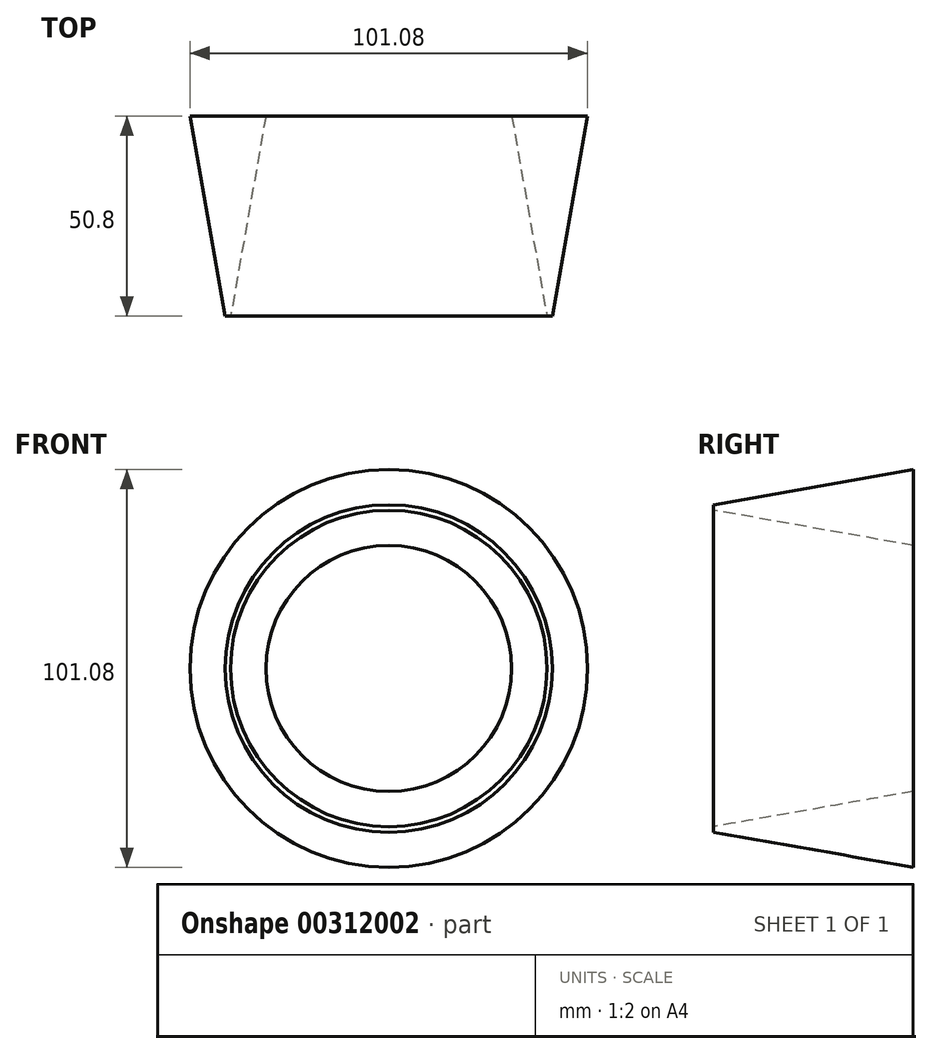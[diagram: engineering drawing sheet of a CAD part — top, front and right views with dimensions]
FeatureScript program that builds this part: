
annotation { "Feature Type Name" : "Feature", "Feature Type Description" : "" }
export const myFeature = defineFeature(function(context is Context, id is Id, definition is map)
    precondition{}
    {
        {
            var Q0;
            Q0=qCreatedBy(makeId("Front.planeOp"),FACE);
            var sketch = newSketch(context, id + "F0", { "sketchPlane" : qUnion([Q0])});
            skCircle(sketch, "E0", {"center": v(-5.39, 0) * mm, "radius": 31.23 * mm});
            skCircle(sketch, "E1", {"center": v(-5.39, 0) * mm, "radius": 50.54 * mm});
            skSolve(sketch);
        }
        {
            var Q0;
            Q0=makeQuery(id+"F0.imprint","IMPRINT",FACE,{"disambiguationData":[TD([[makeQuery(id+"F0.imprint","IMPRINT",EDGE,{"derivedFrom":sQuery(id+"F0.wireOp",EDGE,"E0")}),-1.0]])]});
            extrude(context, id + "F1", {"entities" : qUnion([Q0]), "depth" : 50.8 * mm, "hasDraft" : true, "draftAngle" : 10 * degree, "draftPullDirection" : true});
        }
    });
